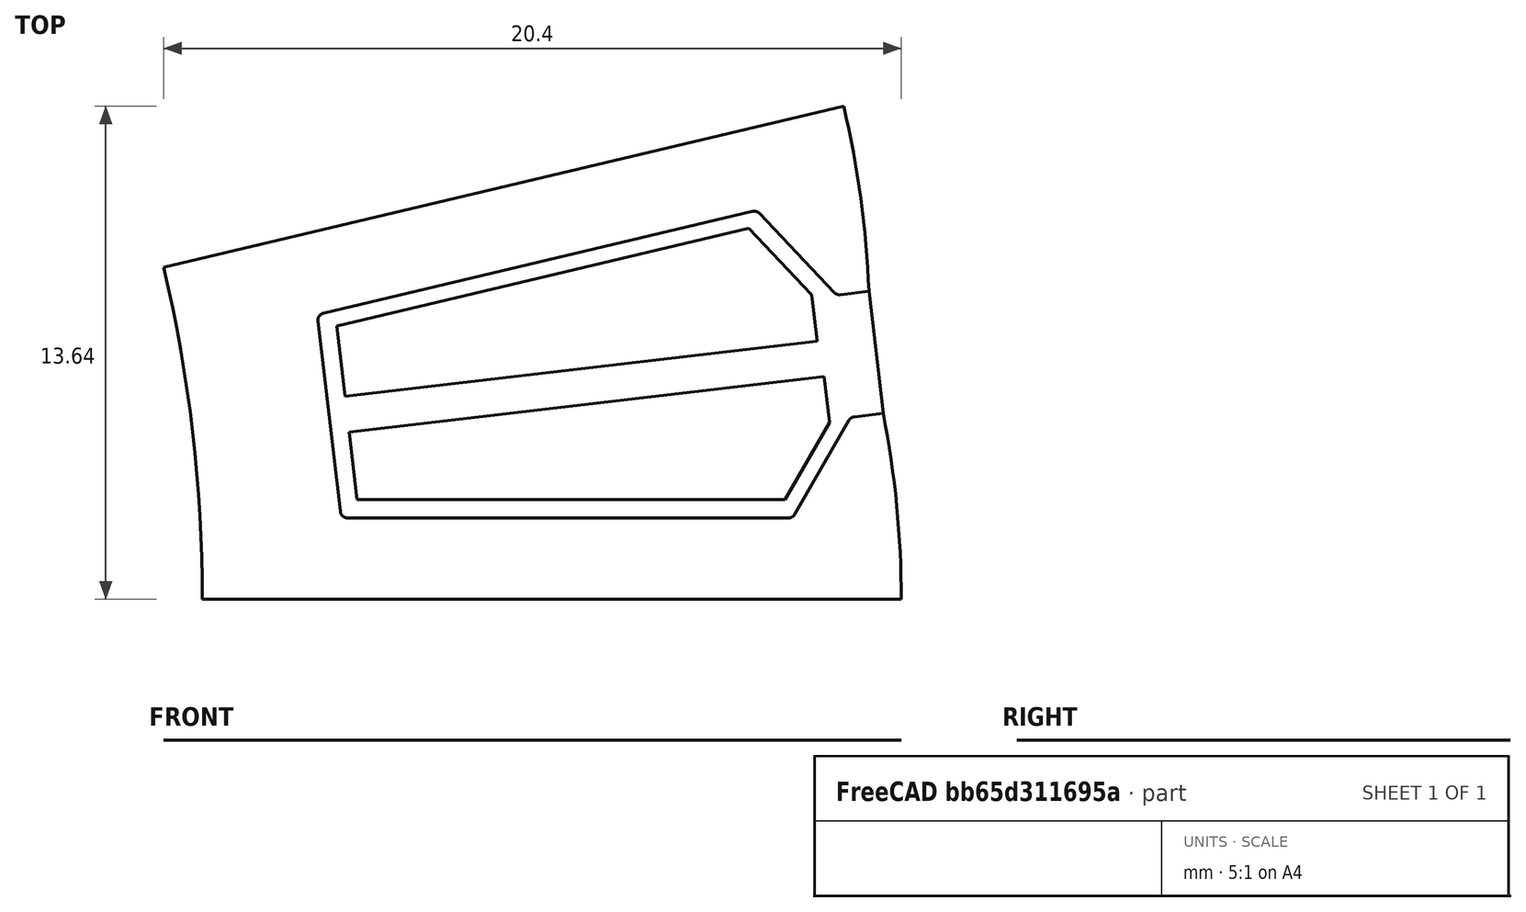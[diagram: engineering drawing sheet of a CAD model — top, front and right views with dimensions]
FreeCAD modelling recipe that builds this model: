
FCSTD DOCUMENT  (FreeCAD 0.18R4 (GitTag))
Label: StatorORNeedleWinding
License: All rights reserved
LicenseURL: http://en.wikipedia.org/wiki/All_rights_reserved
objects: Sketcher::SketchObject×7, Surface::Filling×4, PartDesign::Body×2, Spreadsheet::Sheet×1
note: 13 computed .brp shape members not serialized (recipe doc carries the construction recipe); baked Part::Feature solids carry a one-line shape summary decoded from their .brp

FEATURE [Spreadsheet::Sheet] Spreadsheet  label="Variables"
  cells = A2=slotNumber; B2(slotNumber)=27; A3=outerDiameter; B3(outerDiameter)=118.3; A4=innerDiameter; B4(innerDiameter)=79.59999999999999; A5=stackLength; B5(stackLength)=38; A6=stackingFactor; B6(stackingFactor)=0.95; A7=cuttingThickness; B7(cuttingThickness)=0.1; A8=skewAngle; B8(skewAngle)=0; A9=segmentAngle; B9(segmentAngle)==360 / slotNumber; A10=tipHeightReduction; B10(tipHeightReduction)=25; A11=toothThickness; B11(toothThickness)=4.5; A12=yokeThickness; B12(yokeThickness)=3.8; A13=tipHeight; B13(tipHeight)=1.2; A14=tipAngle; B14(tipAngle)=120; A15=openingLeft; B15(openingLeft)=1.7; A16=openingRight; B16(openingRight)=1.7; A17=slotIsolation; B17(slotIsolation)=0.5; A18=windingAngle; B18(windingAngle)=35; A19=heightRatio; B19(heightRatio)=45; A20=roundingRadii; B20(roundingRadii)=0.2; A21=phaseSeparation; B21(phaseSeparation)=1
FEATURE [Sketcher::SketchObject] Sketch003  label="StatorSketch1"
  MapMode = 5
  Support = -> [XY_Plane]
  expr: Constraints[81] = Variables.roundingRadii
  expr: Constraints[31] = Variables.openingRight
  expr: Constraints[21] = Variables.openingLeft
  expr: Constraints[92] = Variables.tipHeight
  expr: Constraints[53] = Variables.innerDiameter / 2 + Variables.yokeThickness
  expr: Constraints[13] = Variables.innerDiameter / 2
  expr: Constraints[7] = Variables.tipHeight
  expr: Constraints[78] = Variables.roundingRadii
  expr: Constraints[63] = Variables.roundingRadii
  expr: Constraints[20] = 90
  expr: Constraints[45] = Variables.toothThickness / 2
  expr: Constraints[14] = Variables.segmentAngle / 2
  expr: Constraints[41] = Variables.tipAngle
  expr: Constraints[75] = Variables.roundingRadii
  expr: Constraints[95] = Variables.outerDiameter / 2
  expr: Constraints[26] = 90
  expr: Constraints[4] = Variables.tipHeight * (1 - Variables.tipHeightReduction / 100)
  expr: Constraints[40] = Variables.tipAngle
  expr: Constraints[70] = Variables.roundingRadii
  expr: Constraints[33] = Variables.tipHeight * (1 - Variables.tipHeightReduction / 100)
  expr: Constraints[0] = Variables.segmentAngle
  sketch-geometry (37):
    g0: LineSegment [constr] StartX=0 StartY=0 StartZ=0 EndX=57.5318 EndY=13.6353 EndZ=0
    g1: LineSegment [constr] StartX=0 StartY=0 StartZ=0 EndX=59.1256 EndY=-1e-15 EndZ=0
    g2: LineSegment [constr] StartX=0 StartY=0 StartZ=0 EndX=58.7258 EndY=6.86406 EndZ=0
    g3: LineSegment [constr] StartX=56.1413 StartY=18.6247 StartZ=0 EndX=58.5284 EndY=8.55256 EndZ=0
    g4: LineSegment [constr] StartX=58.5284 StartY=8.55256 StartZ=0 EndX=57.4363 EndY=8.42491 EndZ=0
    g5: LineSegment [constr] StartX=57.3365 StartY=8.41325 StartZ=0 EndX=58.2305 EndY=8.51774 EndZ=0
    g6: ArcOfCircle CenterX=31.5942 CenterY=7.48796 CenterZ=0 NormalX=0 NormalY=0 NormalZ=1 AngleXU=0 Radius=26.6562 StartAngle=0.0386415 EndAngle=0.232711
    g7: LineSegment StartX=57.5318 StartY=13.6353 StartZ=0 EndX=38.7272 EndY=9.17851 EndZ=0
    g8: ArcOfCircle CenterX=0 CenterY=0 CenterZ=0 NormalX=0 NormalY=0 NormalZ=1 AngleXU=0 Radius=39.8 StartAngle=0 EndAngle=0.232711
    g9: LineSegment [constr] StartX=58.7258 StartY=6.86406 StartZ=0 EndX=58.5284 EndY=8.55256 EndZ=0
    g10: LineSegment [constr] StartX=58.9231 StartY=5.17555 StartZ=0 EndX=57.831 EndY=5.0479 EndZ=0
    g11: LineSegment [constr] StartX=58.7258 StartY=6.86406 StartZ=0 EndX=58.9231 EndY=5.17555 EndZ=0
    g12: LineSegment [constr] StartX=57.7313 StartY=5.03624 StartZ=0 EndX=58.6252 EndY=5.14073 EndZ=0
    g13: ArcOfCircle CenterX=32.4694 CenterY=-2.41e-14 CenterZ=0 NormalX=0 NormalY=0 NormalZ=1 AngleXU=0 Radius=26.6562 StartAngle=-9e-16 EndAngle=0.194069
    g14: LineSegment StartX=39.8 StartY=-2e-16 StartZ=0 EndX=59.1256 EndY=-1e-15 EndZ=0
    g15: LineSegment StartX=57.2676 StartY=8.48631 StartZ=0 EndX=55.2079 EndY=10.6694 EndZ=0
    g16: LineSegment StartX=55.0163 StartY=10.7268 StartZ=0 EndX=43.1497 EndY=7.91435 EndZ=0
    g17: LineSegment StartX=42.9972 StartY=7.69652 StartZ=0 EndX=43.6132 EndY=2.42678 EndZ=0
    g18: LineSegment StartX=43.8118 StartY=2.25 StartZ=0 EndX=56.0071 EndY=2.25 EndZ=0
    g19: LineSegment StartX=56.1803 StartY=2.35 StartZ=0 EndX=57.681 EndY=4.94926 EndZ=0
    g20: LineSegment [constr] StartX=43.1497 StartY=7.91435 StartZ=0 EndX=42.6309 EndY=10.1037 EndZ=0
    g21: LineSegment [constr] StartX=43.8118 StartY=2.25 StartZ=0 EndX=43.8118 EndY=9e-16 EndZ=0
    g22: LineSegment [constr] StartX=0 StartY=0 StartZ=0 EndX=43.3052 EndY=5.06165 EndZ=0
    g23: LineSegment [constr] StartX=57.3365 StartY=8.41325 StartZ=0 EndX=58.2305 EndY=8.51774 EndZ=0
    g24: LineSegment [constr] StartX=57.7313 StartY=5.03624 StartZ=0 EndX=58.6252 EndY=5.14073 EndZ=0
    g25: ArcOfCircle CenterX=57.4131 CenterY=8.62356 CenterZ=0 NormalX=0 NormalY=0 NormalZ=1 AngleXU=0 Radius=0.2 StartAngle=3.8979 EndAngle=4.82874
    g26: LineSegment [constr] StartX=57.2676 StartY=8.48631 StartZ=0 EndX=57.3365 EndY=8.41325 EndZ=0
    g27: ArcOfCircle CenterX=55.0625 CenterY=10.5322 CenterZ=0 NormalX=0 NormalY=0 NormalZ=1 AngleXU=0 Radius=0.2 StartAngle=0.756309 EndAngle=1.80351
    g28: ArcOfCircle CenterX=43.1959 CenterY=7.71974 CenterZ=0 NormalX=0 NormalY=0 NormalZ=1 AngleXU=0 Radius=0.2 StartAngle=1.80351 EndAngle=3.25795
    g29: ArcOfCircle CenterX=43.8118 CenterY=2.45 CenterZ=0 NormalX=0 NormalY=0 NormalZ=1 AngleXU=0 Radius=0.2 StartAngle=3.25795 EndAngle=4.71239
    g30: ArcOfCircle CenterX=56.0071 CenterY=2.45 CenterZ=0 NormalX=0 NormalY=0 NormalZ=1 AngleXU=0 Radius=0.2 StartAngle=4.71239 EndAngle=5.75959
    g31: ArcOfCircle CenterX=57.8542 CenterY=4.84926 CenterZ=0 NormalX=0 NormalY=0 NormalZ=1 AngleXU=0 Radius=0.2 StartAngle=1.68715 EndAngle=2.61799
    g32: LineSegment [constr] StartX=57.831 StartY=5.0479 StartZ=0 EndX=57.7313 EndY=5.03624 EndZ=0
    g33: LineSegment [constr] StartX=57.7313 StartY=5.03624 StartZ=0 EndX=57.681 EndY=4.94926 EndZ=0
    g34: LineSegment StartX=58.2305 StartY=8.51774 StartZ=0 EndX=57.4363 EndY=8.42491 EndZ=0
    g35: LineSegment StartX=57.831 StartY=5.0479 StartZ=0 EndX=58.6252 EndY=5.14073 EndZ=0
    g36: LineSegment [constr] StartX=0 StartY=0 StartZ=0 EndX=58.5284 EndY=8.55256 EndZ=0
  constraints (96):
    c: Angle(g1,g0) = 0.232711
    c: Symmetric(g3,g3,g0)
    c: Coincident(g4,g3)
    c: PointOnObject(g5,g4)
    c: Distance(g5) = 0.9
    c: Coincident(g6,g5)
    c: PointOnObject(g6,g0)
    c: Distance(g5,g3) = 1.2
    c: Coincident(g7,g6)
    c: PointOnObject(g7,g0)
    c: PointOnObject(g8,g1)
    c: Coincident(g8,g-1)
    c: Coincident(g8,g7)
    c: Radius(g8) = 39.8
    c: Angle(g-1,g2) = 0.116355
    c: Angle(g-1,g1) = 0
    c: Coincident(g2,g8)
    c: Coincident(g0,g8)
    c: Coincident(g9,g2)
    c: Coincident(g9,g3)
    c: Angle(g9,g2) = 1.5708
    c: Distance(g9) = 1.7
    c: Coincident(g6,g0)
    c: Equal(g0,g2)
    c: Equal(g1,g2)
    c: Coincident(g1,g8)
    c: Angle(g4,g9) = 1.5708
    c: Coincident(g11,g2)
    c: Coincident(g11,g10)
    c: Angle(g2,g11) = 1.5708
    c: Angle(g11,g10) = 1.5708
    c: Distance(g11) = 1.7
    c: Angle(g10,g12) = 0
    c: Distance(g12,g12) = 0.9
    c: PointOnObject(g13,g1)
    c: Coincident(g13,g12)
    c: Coincident(g13,g1)
    c: Coincident(g14,g8)
    c: Coincident(g14,g13)
    c: Horizontal(g18)
    c: Angle(g16,g15) = 2.0944
    c: Angle(g19,g18) = 2.0944
    c: PointOnObject(g20,g7)
    c: Angle(g16,g20) = 1.5708
    c: Angle(g20,g0) = 1.5708
    c: Distance(g20) = 2.25
    c: PointOnObject(g21,g14)
    c: Angle(g21,g18) = 1.5708
    c: Equal(g21,g20)
    c: Coincident(g22,g8)
    c: PointOnObject(g22,g17)
    c: Angle(g17,g22) = 1.5708
    c: PointOnObject(g22,g2)
    c: Distance(g8,g22) = 43.6
    c: Coincident(g23,g5)
    c: Coincident(g23,g6)
    c: Coincident(g24,g12)
    c: Coincident(g24,g13)
    c: Tangent(g4,g25) = 1.5708
    c: Tangent(g15,g25) = 1.5708
    c: Coincident(g26,g15)
    c: Coincident(g26,g5)
    c: Parallel(g26,g15)
    c: Radius(g25) = 0.2
    c: PointOnObject(g4,g5)
    c: Tangent(g16,g27) = -1.5708
    c: Tangent(g15,g27) = -1.5708
    c: Equal(g27,g25)
    c: Tangent(g17,g28) = -1.5708
    c: Tangent(g16,g28) = -1.5708
    c: Radius(g28) = 0.2
    c: Coincident(g20,g16)
    c: Tangent(g17,g29) = -1.5708
    c: Tangent(g18,g29) = -1.5708
    c: Coincident(g21,g18)
    c: Radius(g29) = 0.2
    c: Tangent(g18,g30) = -1.5708
    c: Tangent(g19,g30) = -1.5708
    c: Radius(g30) = 0.2
    c: Tangent(g19,g31) = 1.5708
    c: Tangent(g10,g31) = -1.5708
    c: Radius(g31) = 0.2
    c: Coincident(g32,g10)
    c: Coincident(g33,g32)
    c: Coincident(g33,g19)
    c: Parallel(g19,g33)
    c: Parallel(g32,g10)
    c: Coincident(g12,g32)
    c: Coincident(g34,g6)
    c: Coincident(g34,g4)
    c: Coincident(g35,g31)
    c: Coincident(g35,g13)
    c: Distance(g12,g10) = 1.2
    c: Coincident(g36,g8)
    c: Coincident(g36,g3)
    c: Distance(g36) = 59.15
FEATURE [Sketcher::SketchObject] Sketch  label="StatorStack"
  MapMode = 5
  Support = -> [XY_Plane001]
  expr: Constraints[18] = Variables.innerDiameter / 2
  expr: Constraints[10] = Variables.outerDiameter / 2
  expr: Constraints[9] = Variables.innerDiameter / 2
  expr: Constraints[8] = Variables.stackLength
  sketch-geometry (8):
    g0: LineSegment StartX=-19 StartY=39.8 StartZ=0 EndX=19 EndY=39.8 EndZ=0
    g1: LineSegment StartX=19 StartY=39.8 StartZ=0 EndX=19 EndY=59.15 EndZ=0
    g2: LineSegment StartX=19 StartY=59.15 StartZ=0 EndX=-19 EndY=59.15 EndZ=0
    g3: LineSegment StartX=-19 StartY=59.15 StartZ=0 EndX=-19 EndY=39.8 EndZ=0
    g4: LineSegment StartX=-19 StartY=-39.8 StartZ=0 EndX=19 EndY=-39.8 EndZ=0
    g5: LineSegment StartX=19 StartY=-39.8 StartZ=0 EndX=19 EndY=-59.15 EndZ=0
    g6: LineSegment StartX=19 StartY=-59.15 StartZ=0 EndX=-19 EndY=-59.15 EndZ=0
    g7: LineSegment StartX=-19 StartY=-59.15 StartZ=0 EndX=-19 EndY=-39.8 EndZ=0
  constraints (22):
    c: Coincident(g0,g1)
    c: Coincident(g1,g2)
    c: Coincident(g2,g3)
    c: Coincident(g3,g0)
    c: Horizontal(g2)
    c: Vertical(g1)
    c: Vertical(g3)
    c: Symmetric(g0,g0,g-2)
    c: DistanceX(g0,g0) = 38
    c: DistanceY(g-1,g0) = 39.8
    c: DistanceY(g-1,g1) = 59.15
    c: Coincident(g4,g5)
    c: Coincident(g5,g6)
    c: Coincident(g6,g7)
    c: Coincident(g7,g4)
    c: Horizontal(g6)
    c: Equal(g4,g0)
    c: Symmetric(g4,g4,g-2)
    c: DistanceY(g4,g-1) = 39.8
    c: Equal(g7,g3)
    c: Angle(g7,g4) = 1.5708
    c: Angle(g4,g5) = 1.5708
FEATURE [PartDesign::Body] Body001  label="SideView"
  Group = -> [Sketch]
  Origin = -> Origin001
FEATURE [Sketcher::SketchObject] Sketch004  label="SlotSketch"
  MapMode = 5
  Support = -> [XY_Plane]
  expr: Constraints[81] = Variables.roundingRadii
  expr: Constraints[31] = Variables.openingRight
  expr: Constraints[21] = Variables.openingLeft
  expr: Constraints[53] = Variables.innerDiameter / 2 + Variables.yokeThickness
  expr: Constraints[7] = Variables.tipHeight
  expr: Constraints[13] = Variables.innerDiameter / 2
  expr: Constraints[78] = Variables.roundingRadii
  expr: Constraints[63] = Variables.roundingRadii
  expr: Constraints[20] = 90
  expr: Constraints[45] = Variables.toothThickness / 2
  expr: Constraints[14] = Variables.segmentAngle / 2
  expr: Constraints[41] = Variables.tipAngle
  expr: Constraints[75] = Variables.roundingRadii
  expr: Constraints[26] = 90
  expr: Constraints[4] = Variables.tipHeight * (1 - Variables.tipHeightReduction / 100)
  expr: Constraints[40] = Variables.tipAngle
  expr: Constraints[94] = Variables.tipHeight
  expr: Constraints[70] = Variables.roundingRadii
  expr: Constraints[97] = Variables.outerDiameter / 2
  expr: Constraints[0] = Variables.segmentAngle
  expr: Constraints[33] = Variables.tipHeight * (1 - Variables.tipHeightReduction / 100)
  sketch-geometry (38):
    g0: LineSegment [constr] StartX=0 StartY=0 StartZ=0 EndX=57.5318 EndY=13.6353 EndZ=0
    g1: LineSegment [constr] StartX=0 StartY=0 StartZ=0 EndX=59.1256 EndY=0 EndZ=0
    g2: LineSegment [constr] StartX=0 StartY=0 StartZ=0 EndX=58.7258 EndY=6.86406 EndZ=0
    g3: LineSegment [constr] StartX=56.1413 StartY=18.6247 StartZ=0 EndX=58.5284 EndY=8.55256 EndZ=0
    g4: LineSegment [constr] StartX=58.5284 StartY=8.55256 StartZ=0 EndX=57.4363 EndY=8.42491 EndZ=0
    g5: LineSegment [constr] StartX=57.3365 StartY=8.41325 StartZ=0 EndX=58.2305 EndY=8.51774 EndZ=0
    g6: ArcOfCircle [constr] CenterX=31.5942 CenterY=7.48796 CenterZ=0 NormalX=0 NormalY=0 NormalZ=1 AngleXU=0 Radius=26.6562 StartAngle=0.0386415 EndAngle=0.232711
    g7: LineSegment [constr] StartX=57.5318 StartY=13.6353 StartZ=0 EndX=38.7272 EndY=9.17851 EndZ=0
    g8: ArcOfCircle [constr] CenterX=0 CenterY=0 CenterZ=0 NormalX=0 NormalY=0 NormalZ=1 AngleXU=0 Radius=39.8 StartAngle=0 EndAngle=0.232711
    g9: LineSegment [constr] StartX=58.7258 StartY=6.86406 StartZ=0 EndX=58.5284 EndY=8.55256 EndZ=0
    g10: LineSegment [constr] StartX=58.9231 StartY=5.17555 StartZ=0 EndX=57.831 EndY=5.0479 EndZ=0
    g11: LineSegment [constr] StartX=58.7258 StartY=6.86406 StartZ=0 EndX=58.9231 EndY=5.17555 EndZ=0
    g12: LineSegment [constr] StartX=57.7313 StartY=5.03624 StartZ=0 EndX=58.6252 EndY=5.14073 EndZ=0
    g13: ArcOfCircle [constr] CenterX=32.4694 CenterY=0 CenterZ=0 NormalX=0 NormalY=0 NormalZ=1 AngleXU=0 Radius=26.6562 StartAngle=0 EndAngle=0.194069
    g14: LineSegment [constr] StartX=39.8 StartY=0 StartZ=0 EndX=59.1256 EndY=0 EndZ=0
    g15: LineSegment StartX=57.2676 StartY=8.48631 StartZ=0 EndX=55.2079 EndY=10.6694 EndZ=0
    g16: LineSegment StartX=55.0163 StartY=10.7268 StartZ=0 EndX=43.1497 EndY=7.91435 EndZ=0
    g17: LineSegment StartX=42.9972 StartY=7.69652 StartZ=0 EndX=43.6132 EndY=2.42678 EndZ=0
    g18: LineSegment StartX=43.8118 StartY=2.25 StartZ=0 EndX=56.0071 EndY=2.25 EndZ=0
    g19: LineSegment StartX=56.1803 StartY=2.35 StartZ=0 EndX=57.681 EndY=4.94926 EndZ=0
    g20: LineSegment [constr] StartX=43.1497 StartY=7.91435 StartZ=0 EndX=42.6309 EndY=10.1037 EndZ=0
    g21: LineSegment [constr] StartX=43.8118 StartY=2.25 StartZ=0 EndX=43.8118 EndY=0 EndZ=0
    g22: LineSegment [constr] StartX=0 StartY=0 StartZ=0 EndX=43.3052 EndY=5.06165 EndZ=0
    g23: LineSegment [constr] StartX=57.3365 StartY=8.41325 StartZ=0 EndX=58.2305 EndY=8.51774 EndZ=0
    g24: LineSegment [constr] StartX=57.7313 StartY=5.03624 StartZ=0 EndX=58.6252 EndY=5.14073 EndZ=0
    g25: ArcOfCircle CenterX=57.4131 CenterY=8.62356 CenterZ=0 NormalX=0 NormalY=0 NormalZ=1 AngleXU=0 Radius=0.2 StartAngle=3.8979 EndAngle=4.82874
    g26: LineSegment [constr] StartX=57.2676 StartY=8.48631 StartZ=0 EndX=57.3365 EndY=8.41325 EndZ=0
    g27: ArcOfCircle CenterX=55.0625 CenterY=10.5322 CenterZ=0 NormalX=0 NormalY=0 NormalZ=1 AngleXU=0 Radius=0.2 StartAngle=0.756309 EndAngle=1.80351
    g28: ArcOfCircle CenterX=43.1959 CenterY=7.71974 CenterZ=0 NormalX=0 NormalY=0 NormalZ=1 AngleXU=0 Radius=0.2 StartAngle=1.80351 EndAngle=3.25795
    g29: ArcOfCircle CenterX=43.8118 CenterY=2.45 CenterZ=0 NormalX=0 NormalY=0 NormalZ=1 AngleXU=0 Radius=0.2 StartAngle=3.25795 EndAngle=4.71239
    g30: ArcOfCircle CenterX=56.0071 CenterY=2.45 CenterZ=0 NormalX=0 NormalY=0 NormalZ=1 AngleXU=0 Radius=0.2 StartAngle=4.71239 EndAngle=5.75959
    g31: ArcOfCircle CenterX=57.8542 CenterY=4.84926 CenterZ=0 NormalX=0 NormalY=0 NormalZ=1 AngleXU=0 Radius=0.2 StartAngle=1.68715 EndAngle=2.61799
    g32: LineSegment [constr] StartX=57.831 StartY=5.0479 StartZ=0 EndX=57.7313 EndY=5.03624 EndZ=0
    g33: LineSegment [constr] StartX=57.7313 StartY=5.03624 StartZ=0 EndX=57.681 EndY=4.94926 EndZ=0
    g34: LineSegment StartX=58.2305 StartY=8.51774 StartZ=0 EndX=57.4363 EndY=8.42491 EndZ=0
    g35: LineSegment StartX=57.831 StartY=5.0479 StartZ=0 EndX=58.6252 EndY=5.14073 EndZ=0
    g36: LineSegment StartX=58.2305 StartY=8.51774 StartZ=0 EndX=58.6252 EndY=5.14073 EndZ=0
    g37: LineSegment [constr] StartX=0 StartY=0 StartZ=0 EndX=58.5284 EndY=8.55256 EndZ=0
  constraints (98):
    c: Angle(g1,g0) = 0.232711
    c: Symmetric(g3,g3,g0)
    c: Coincident(g4,g3)
    c: PointOnObject(g5,g4)
    c: Distance(g5) = 0.9
    c: Coincident(g6,g5)
    c: PointOnObject(g6,g0)
    c: Distance(g5,g3) = 1.2
    c: Coincident(g7,g6)
    c: PointOnObject(g7,g0)
    c: PointOnObject(g8,g1)
    c: Coincident(g8,g-1)
    c: Coincident(g8,g7)
    c: Radius(g8) = 39.8
    c: Angle(g-1,g2) = 0.116355
    c: Angle(g-1,g1) = 0
    c: Coincident(g2,g8)
    c: Coincident(g0,g8)
    c: Coincident(g9,g2)
    c: Coincident(g9,g3)
    c: Angle(g9,g2) = 1.5708
    c: Distance(g9) = 1.7
    c: Coincident(g6,g0)
    c: Equal(g0,g2)
    c: Equal(g1,g2)
    c: Coincident(g1,g8)
    c: Angle(g4,g9) = 1.5708
    c: Coincident(g11,g2)
    c: Coincident(g11,g10)
    c: Angle(g2,g11) = 1.5708
    c: Angle(g11,g10) = 1.5708
    c: Distance(g11) = 1.7
    c: Angle(g10,g12) = 0
    c: Distance(g12,g12) = 0.9
    c: PointOnObject(g13,g1)
    c: Coincident(g13,g12)
    c: Coincident(g13,g1)
    c: Coincident(g14,g8)
    c: Coincident(g14,g13)
    c: Horizontal(g18)
    c: Angle(g16,g15) = 2.0944
    c: Angle(g19,g18) = 2.0944
    c: PointOnObject(g20,g7)
    c: Angle(g16,g20) = 1.5708
    c: Angle(g20,g0) = 1.5708
    c: Distance(g20) = 2.25
    c: PointOnObject(g21,g14)
    c: Angle(g21,g18) = 1.5708
    c: Equal(g21,g20)
    c: Coincident(g22,g8)
    c: PointOnObject(g22,g17)
    c: Angle(g17,g22) = 1.5708
    c: PointOnObject(g22,g2)
    c: Distance(g8,g22) = 43.6
    c: Coincident(g23,g5)
    c: Coincident(g23,g6)
    c: Coincident(g24,g12)
    c: Coincident(g24,g13)
    c: Tangent(g4,g25) = 1.5708
    c: Tangent(g15,g25) = 1.5708
    c: Coincident(g26,g15)
    c: Coincident(g26,g5)
    c: Parallel(g26,g15)
    c: Radius(g25) = 0.2
    c: PointOnObject(g4,g5)
    c: Tangent(g16,g27) = -1.5708
    c: Tangent(g15,g27) = -1.5708
    c: Equal(g27,g25)
    c: Tangent(g17,g28) = -1.5708
    c: Tangent(g16,g28) = -1.5708
    c: Radius(g28) = 0.2
    c: Coincident(g20,g16)
    c: Tangent(g17,g29) = -1.5708
    c: Tangent(g18,g29) = -1.5708
    c: Coincident(g21,g18)
    c: Radius(g29) = 0.2
    c: Tangent(g18,g30) = -1.5708
    c: Tangent(g19,g30) = -1.5708
    c: Radius(g30) = 0.2
    c: Tangent(g19,g31) = 1.5708
    c: Tangent(g10,g31) = -1.5708
    c: Radius(g31) = 0.2
    c: Coincident(g32,g10)
    c: Coincident(g33,g32)
    c: Coincident(g33,g19)
    c: Parallel(g19,g33)
    c: Parallel(g32,g10)
    c: Coincident(g12,g32)
    c: Coincident(g34,g6)
    c: Coincident(g34,g4)
    c: Coincident(g35,g31)
    c: Coincident(g35,g13)
    c: Coincident(g36,g34)
    c: Coincident(g36,g35)
    c: Distance(g12,g10) = 1.2
    c: Coincident(g37,g-1)
    c: Coincident(g37,g3)
    c: Distance(g37) = 59.15
FEATURE [Surface::Filling] Surface  label="SlotSketch_Surface"
  Anisotropy = false
  BoundaryEdges = -> [Sketch004]
  BoundaryOrder = [0,0,0,0,0,0,0,0,0,0,0,0,0,0]
  Degree = 3
  Iterations = 2
  MaximumDegree = 8
  MaximumSegments = 9
  PointsOnCurve = 15
  TolAngular = 0.01
  TolCurvature = 0.1
  Tolerance2d = 1e-05
  Tolerance3d = 0.0001
FEATURE [Sketcher::SketchObject] Sketch005  label="TerminalLeftSketch"
  ExternalGeometry = -> [Sketch003]
  MapMode = 5
  Support = -> [XY_Plane]
  expr: Constraints[32] = Variables.phaseSeparation / 2
  expr: Constraints[28] = Variables.segmentAngle / 2
  expr: Constraints[16] = Variables.slotIsolation
  sketch-geometry (12):
    g0: LineSegment StartX=56.6485 StartY=8.41395 StartZ=0 EndX=54.91 EndY=10.2566 EndZ=0
    g1: LineSegment StartX=54.91 StartY=10.2566 StartZ=0 EndX=43.517 EndY=7.55638 EndZ=0
    g2: LineSegment StartX=43.517 StartY=7.55638 StartZ=0 EndX=43.7438 EndY=5.61632 EndZ=0
    g3: LineSegment StartX=43.7438 StartY=5.61632 StartZ=0 EndX=56.7971 EndY=7.14204 EndZ=0
    g4: LineSegment StartX=56.7971 StartY=7.14204 StartZ=0 EndX=56.6485 EndY=8.41395 EndZ=0
    g5: LineSegment [constr] StartX=54.91 StartY=10.2566 StartZ=0 EndX=55.2737 EndY=10.5997 EndZ=0
    g6: LineSegment [constr] StartX=54.91 StartY=10.2566 StartZ=0 EndX=54.5669 EndY=10.6203 EndZ=0
    g7: LineSegment [constr] StartX=43.517 StartY=7.55638 StartZ=0 EndX=43.0204 EndY=7.49834 EndZ=0
    g8: LineSegment [constr] StartX=56.6485 StartY=8.41395 StartZ=0 EndX=57.2676 EndY=8.48631 EndZ=0
    g9: LineSegment [constr] StartX=57.2676 StartY=8.48631 StartZ=0 EndX=57.681 EndY=4.94926 EndZ=0
    g10: LineSegment [constr] StartX=0 StartY=0 StartZ=0 EndX=57.4743 EndY=6.71778 EndZ=0
    g11: LineSegment [constr] StartX=56.7971 StartY=7.14204 StartZ=0 EndX=56.8552 EndY=6.64542 EndZ=0
  constraints (34):
    c: Coincident(g1,g0)
    c: Coincident(g2,g1)
    c: Coincident(g3,g2)
    c: Coincident(g4,g3)
    c: Coincident(g4,g0)
    c: Parallel(g0,g-3)
    c: Parallel(g-4,g1)
    c: Parallel(g2,g-5)
    c: Angle(g3,g2) = 1.5708
    c: Coincident(g5,g0)
    c: PointOnObject(g5,g-3)
    c: Coincident(g6,g0)
    c: PointOnObject(g6,g-4)
    c: Angle(g5,g6) = 1.5708
    c: Angle(g0,g5) = 1.5708
    c: Equal(g6,g5)
    c: Distance(g6) = 0.5
    c: Coincident(g7,g1)
    c: PointOnObject(g7,g-5)
    c: Angle(g7,g2) = 1.5708
    c: Equal(g7,g6)
    c: Coincident(g8,g0)
    c: Coincident(g8,g-3)
    c: Parallel(g4,g2)
    c: Coincident(g9,g8)
    c: Coincident(g9,g-7)
    c: Coincident(g10,g-1)
    c: PointOnObject(g10,g9)
    c: Angle(g-1,g10) = 0.116355
    c: Coincident(g11,g3)
    c: PointOnObject(g11,g10)
    c: Angle(g11,g10) = 1.5708
    c: Distance(g11) = 0.5
    c: Angle(g8,g9) = 1.5708
FEATURE [Sketcher::SketchObject] Sketch006  label="TerminalRightSketch"
  ExternalGeometry = -> [Sketch003]
  MapMode = 5
  Support = -> [XY_Plane]
  expr: Constraints[32] = Variables.phaseSeparation / 2
  expr: Constraints[3] = Variables.segmentAngle / 2
  expr: Constraints[24] = Variables.slotIsolation
  sketch-geometry (12):
    g0: LineSegment [constr] StartX=57.2676 StartY=8.48631 StartZ=0 EndX=57.681 EndY=4.94926 EndZ=0
    g1: LineSegment [constr] StartX=0 StartY=0 StartZ=0 EndX=57.4743 EndY=6.71778 EndZ=0
    g2: LineSegment StartX=57.1448 StartY=4.88658 StartZ=0 EndX=55.9113 EndY=2.75 EndZ=0
    g3: LineSegment StartX=55.9113 StartY=2.75 StartZ=0 EndX=44.0788 EndY=2.75 EndZ=0
    g4: LineSegment StartX=44.0788 StartY=2.75 StartZ=0 EndX=43.8599 EndY=4.62308 EndZ=0
    g5: LineSegment StartX=43.8599 StartY=4.62308 StartZ=0 EndX=56.9962 EndY=6.15849 EndZ=0
    g6: LineSegment StartX=56.9962 StartY=6.15849 StartZ=0 EndX=57.1448 EndY=4.88658 EndZ=0
    g7: LineSegment [constr] StartX=57.1448 StartY=4.88658 StartZ=0 EndX=57.681 EndY=4.94926 EndZ=0
    g8: LineSegment [constr] StartX=55.9113 StartY=2.75 StartZ=0 EndX=56.4113 EndY=2.75 EndZ=0
    g9: LineSegment [constr] StartX=55.9113 StartY=2.75 StartZ=0 EndX=55.9113 EndY=2.25 EndZ=0
    g10: LineSegment [constr] StartX=43.8599 StartY=4.62308 StartZ=0 EndX=43.3632 EndY=4.56503 EndZ=0
    g11: LineSegment [constr] StartX=56.9962 StartY=6.15849 StartZ=0 EndX=56.9381 EndY=6.65511 EndZ=0
  constraints (34):
    c: Coincident(g0,g-7)
    c: Coincident(g1,g-1)
    c: PointOnObject(g1,g0)
    c: Angle(g-1,g1) = 0.116355
    c: Coincident(g3,g2)
    c: Horizontal(g3)
    c: Coincident(g4,g3)
    c: Coincident(g5,g4)
    c: Coincident(g6,g5)
    c: Coincident(g6,g2)
    c: Parallel(g2,g-7)
    c: Parallel(g4,g-5)
    c: Parallel(g5,g1)
    c: Coincident(g0,g-3)
    c: Coincident(g7,g2)
    c: Coincident(g7,g0)
    c: Angle(g0,g7) = 1.5708
    c: Coincident(g8,g2)
    c: PointOnObject(g8,g-7)
    c: Coincident(g9,g2)
    c: PointOnObject(g9,g-6)
    c: Angle(g9,g8) = 1.5708
    c: Equal(g9,g8)
    c: Angle(g3,g9) = 1.5708
    c: Distance(g9) = 0.5
    c: Coincident(g10,g4)
    c: PointOnObject(g10,g-5)
    c: Angle(g10,g4) = 1.5708
    c: Equal(g10,g9)
    c: Coincident(g11,g5)
    c: PointOnObject(g11,g1)
    c: Angle(g1,g11) = 1.5708
    c: Distance(g11) = 0.5
    c: Parallel(g6,g0)
FEATURE [Sketcher::SketchObject] Sketch007  label="YokeLine"
  ExternalGeometry = -> [Sketch003]
  MapMode = 5
  Support = -> [XY_Plane]
  expr: Constraints[2] = Variables.yokeThickness
  sketch-geometry (1):
    g0: LineSegment StartX=43.3052 StartY=5.06165 StartZ=0 EndX=39.5309 EndY=4.6205 EndZ=0
  constraints (3):
    c: Symmetric(g-3,g-3,g0)
    c: Angle(g0,g-3) = 1.5708
    c: Distance(g0) = 3.8
FEATURE [Sketcher::SketchObject] Sketch008  label="ToothLine"
  ExternalGeometry = -> [Sketch003]
  MapMode = 5
  Support = -> [XY_Plane]
  expr: Constraints[2] = Variables.toothThickness
  sketch-geometry (1):
    g0: LineSegment StartX=49.083 StartY=9.32057 StartZ=0 EndX=48.0453 EndY=13.6993 EndZ=0
  constraints (3):
    c: Symmetric(g-3,g-3,g0)
    c: Angle(g-3,g0) = 1.5708
    c: Distance(g0) = 4.5
FEATURE [PartDesign::Body] Body  label="TopView"
  Group = -> [Sketch003,Sketch004,Sketch005,Sketch006,Sketch007,Sketch008]
  Origin = -> Origin
FEATURE [Surface::Filling] Surface001  label="TerminalLeftSketch_Surface"
  Anisotropy = false
  BoundaryEdges = -> [Sketch005]
  BoundaryOrder = [0,0,0,0,0]
  Degree = 3
  Iterations = 2
  MaximumDegree = 8
  MaximumSegments = 9
  PointsOnCurve = 15
  TolAngular = 0.01
  TolCurvature = 0.1
  Tolerance2d = 1e-05
  Tolerance3d = 0.0001
FEATURE [Surface::Filling] Surface002  label="TerminalRightSketch_Surface"
  Anisotropy = false
  BoundaryEdges = -> [Sketch006]
  BoundaryOrder = [0,0,0,0,0]
  Degree = 3
  Iterations = 2
  MaximumDegree = 8
  MaximumSegments = 9
  PointsOnCurve = 15
  TolAngular = 0.01
  TolCurvature = 0.1
  Tolerance2d = 1e-05
  Tolerance3d = 0.0001
FEATURE [Surface::Filling] Surface003  label="StatorSketch1_Surface"
  Anisotropy = false
  BoundaryEdges = -> [Sketch003]
  BoundaryOrder = [0,0,0,0,0,0,0,0,0,0,0,0,0,0,0,0,0,0]
  Degree = 3
  Iterations = 2
  MaximumDegree = 8
  MaximumSegments = 9
  PointsOnCurve = 15
  TolAngular = 0.01
  TolCurvature = 0.1
  Tolerance2d = 1e-05
  Tolerance3d = 0.0001
